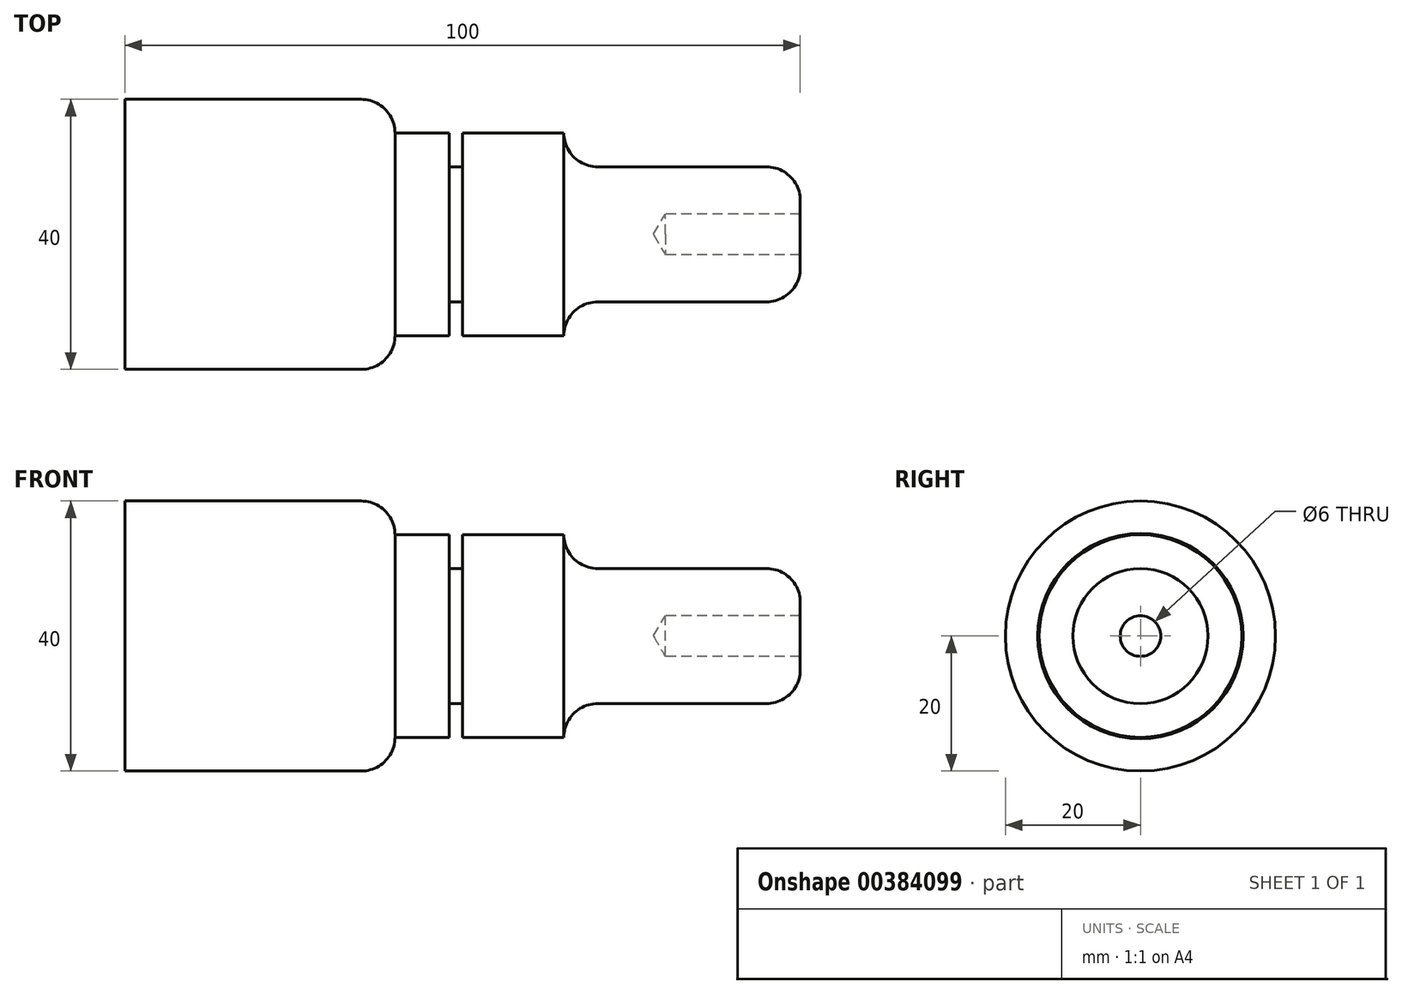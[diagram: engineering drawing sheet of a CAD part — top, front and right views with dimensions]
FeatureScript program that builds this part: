
annotation { "Feature Type Name" : "Feature", "Feature Type Description" : "" }
export const myFeature = defineFeature(function(context is Context, id is Id, definition is map)
    precondition{}
    {
        {
            var Q0;
            Q0=qCreatedBy(makeId("Front.planeOp"),FACE);
            var sketch = newSketch(context, id + "F0", { "sketchPlane" : qUnion([Q0])});
            skLineSegment(sketch, "E0", {"start": v(0, 0) * mm, "end": v(0, 5) * mm});
            skLineSegment(sketch, "E1", {"start": v(-5, 10) * mm, "end": v(-29.8, 10) * mm});
            skLineSegment(sketch, "E2", {"start": v(-35, 15) * mm, "end": v(-50, 15) * mm});
            skLineSegment(sketch, "E3", {"start": v(-60, 15) * mm, "end": v(-60, 15.2) * mm});
            skLineSegment(sketch, "E4", {"start": v(-65, 20) * mm, "end": v(-100, 20) * mm});
            skLineSegment(sketch, "E5", {"start": v(-100, 20) * mm, "end": v(-100, 0) * mm});
            skLineSegment(sketch, "E6", {"start": v(-100, 0) * mm, "end": v(0, 0) * mm});
            skPoint(sketch, "E7.visualSharp", {"position": v(-60, 15) * mm});
            skArc(sketch, "E7.filletArc", {"start": v(-60, 15.2) * mm, "mid": v(-59.94, 15.06) * mm, "end": v(-59.8, 15) * mm});
            skPoint(sketch, "E8.visualSharp", {"position": v(-30, 10) * mm});
            skPoint(sketch, "E9.visualSharp", {"position": v(-60, 20) * mm});
            skArc(sketch, "E9.filletArc", {"start": v(-60, 15) * mm, "mid": v(-61.46, 18.54) * mm, "end": v(-65, 20) * mm});
            skPoint(sketch, "E10.visualSharp", {"position": v(-30, 15) * mm});
            skPoint(sketch, "E11.visualSharp", {"position": v(0, 10) * mm});
            skArc(sketch, "E11.filletArc", {"start": v(0, 5) * mm, "mid": v(-1.46, 8.54) * mm, "end": v(-5, 10) * mm});
            skLineSegment(sketch, "E12", {"start": v(0, 3) * mm, "end": v(-20, 3) * mm});
            skLineSegment(sketch, "E13", {"start": v(-20, 3) * mm, "end": v(-21.73, 0) * mm});
            skLineSegment(sketch, "E14.MirrorCS", {"start": v(0, -3) * mm, "end": v(-20, -3) * mm});
            skLineSegment(sketch, "E15.MirrorCS", {"start": v(-20, -3) * mm, "end": v(-21.73, 0) * mm});
            skArc(sketch, "E16", {"start": v(-35, 15) * mm, "mid": v(-33.54, 11.46) * mm, "end": v(-30, 10) * mm});
            skLineSegment(sketch, "E17", {"start": v(-29.8, 10) * mm, "end": v(-30, 10) * mm});
            skLineSegment(sketch, "E18.right", {"start": v(-50, 15) * mm, "end": v(-50, 10) * mm});
            skLineSegment(sketch, "E19", {"start": v(-50, 10) * mm, "end": v(-52, 10) * mm});
            skLineSegment(sketch, "E20", {"start": v(-52, 10) * mm, "end": v(-52, 15) * mm});
            skLineSegment(sketch, "E21.trimOffspring", {"start": v(-52, 15) * mm, "end": v(-59.8, 15) * mm});
            skSolve(sketch);
        }
        {
            var Q0;
            Q0=makeQuery(id+"F0.imprint","IMPRINT",FACE,{"disambiguationData":[TD([[makeQuery(id+"F0.imprint","IMPRINT",EDGE,{"derivedFrom":sQuery(id+"F0.wireOp",EDGE,"E1")}),1.0]])]});
            var Q1;
            Q1=sQuery(id+"F0.wireOp",EDGE,"E6");
            revolve(context, id + "F1", {"entities" : qUnion([Q0]), "axis" : qUnion([Q1]), "revolveType" : RevolveType.FULL});
        }
    });
